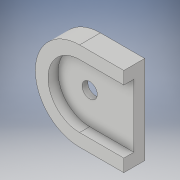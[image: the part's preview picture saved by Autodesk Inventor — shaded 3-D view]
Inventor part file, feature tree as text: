
AUTODESK INVENTOR PART (.ipt)
format: ipt  version: 2017 (Build 210142000, 142)  size: 127,488 bytes
history: native  units: in
note: dims shown in document units (in); Inventor stores cm internally (conversion verified against a paired STEP export)
features: extrude x4, sketch x4
ambient origin geometry x8: Origin, YZ Plane, XZ Plane, XY Plane, X Axis, Y Axis, Z Axis, Center Point
bodies: Solid1 (feature_tree)
feature tree (8):
  extrude  "Extrusion1"  Depth=1.75in
  extrude  "Extrusion2"  Depth=0.825in TaperAngle=0.0deg
  extrude  "Extrusion3"  Depth=2.5in
  extrude  "Extrusion4"  Depth=0.4in TaperAngle=0.0deg
  sketch  "Sketch1"  dims[d0=3.5in d1=1.75in]
  sketch  "Sketch2"  dims[d2=3.5in d3=0.825in d4=0.0in]
  sketch  "Sketch3"  dims[d5=2.5in d6=2.5in]
  sketch  "Sketch4"  dims[d7=1.75in d8=0.4in d9=0.0in d10=0.6in d11=0.2in d12=0.0in d13=1.2in d14=0.2in d15=0.0in]
